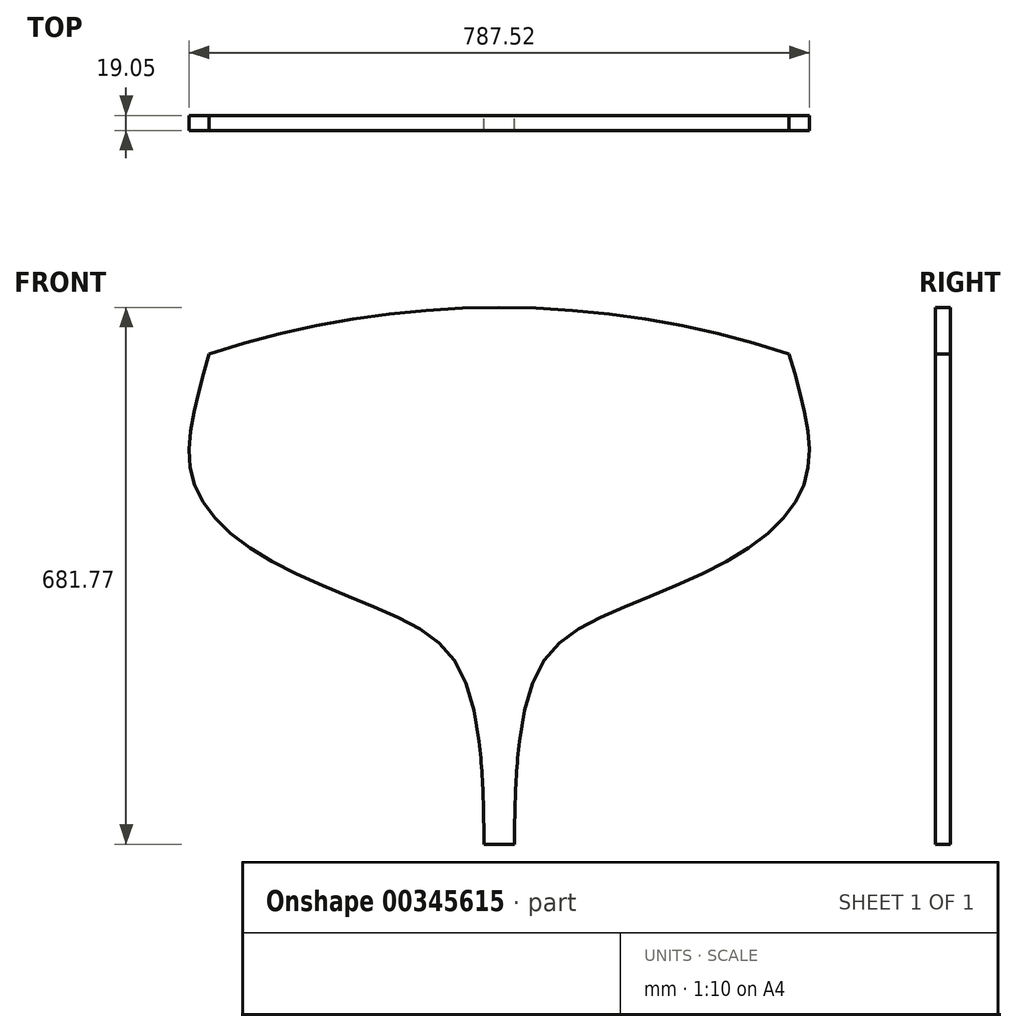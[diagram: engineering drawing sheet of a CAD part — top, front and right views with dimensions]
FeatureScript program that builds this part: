
annotation { "Feature Type Name" : "Feature", "Feature Type Description" : "" }
export const myFeature = defineFeature(function(context is Context, id is Id, definition is map)
    precondition{}
    {
        {
            var Q0;
            Q0=qCreatedBy(makeId("Front.planeOp"),FACE);
            var sketch = newSketch(context, id + "F0", { "sketchPlane" : qUnion([Q0])});
            skLineSegment(sketch, "E0.right", {"start": v(19.12, -0.34) * mm, "end": v(19.12, 130.21) * mm});
            skLineSegment(sketch, "E1.MirrorCS", {"start": v(-19.12, -0.34) * mm, "end": v(-19.12, 130.21) * mm});
            skFitSpline(sketch, "E2", {"points": [v(-19.12, -0.34) * mm, v(-53.98, 228.6) * mm, v(-168.27, 304.8) * mm, v(-323.85, 381) * mm, v(-387.35, 457.2) * mm, v(-390.53, 533.4) * mm, v(-368.3, 622.3) * mm], "startDerivative": vector(-21.06, 1196.95) * mm, "endDerivative": vector(187.46, 642.19) * mm});
            skFitSpline(sketch, "E3.MirrorCS", {"points": [v(19.12, -0.34) * mm, v(53.97, 228.6) * mm, v(168.28, 304.8) * mm, v(323.85, 381) * mm, v(387.35, 457.2) * mm, v(390.53, 533.4) * mm, v(368.3, 622.3) * mm], "startDerivative": vector(21.06, 1196.95) * mm, "endDerivative": vector(-187.46, 642.19) * mm});
            skArc(sketch, "E4", {"start": v(368.3, 622.3) * mm, "mid": v(0, 681.43) * mm, "end": v(-368.3, 622.3) * mm});
            skLineSegment(sketch, "E5", {"start": v(25.47, 130.21) * mm, "end": v(-25.47, 130.21) * mm});
            skPoint(sketch, "E6", {"position": v(-25.47, 130.21) * mm});
            skPoint(sketch, "E7", {"position": v(25.47, 130.21) * mm});
            skLineSegment(sketch, "E8", {"start": v(-19.12, -0.34) * mm, "end": v(19.12, -0.34) * mm});
            skSolve(sketch);
        }
        {
            var Q0;
            Q0 = qSketchRegion(id + "F0", true);
            extrude(context, id + "F1", {"entities" : qUnion([Q0]), "depth" : 19.05 * mm});
        }
    });
